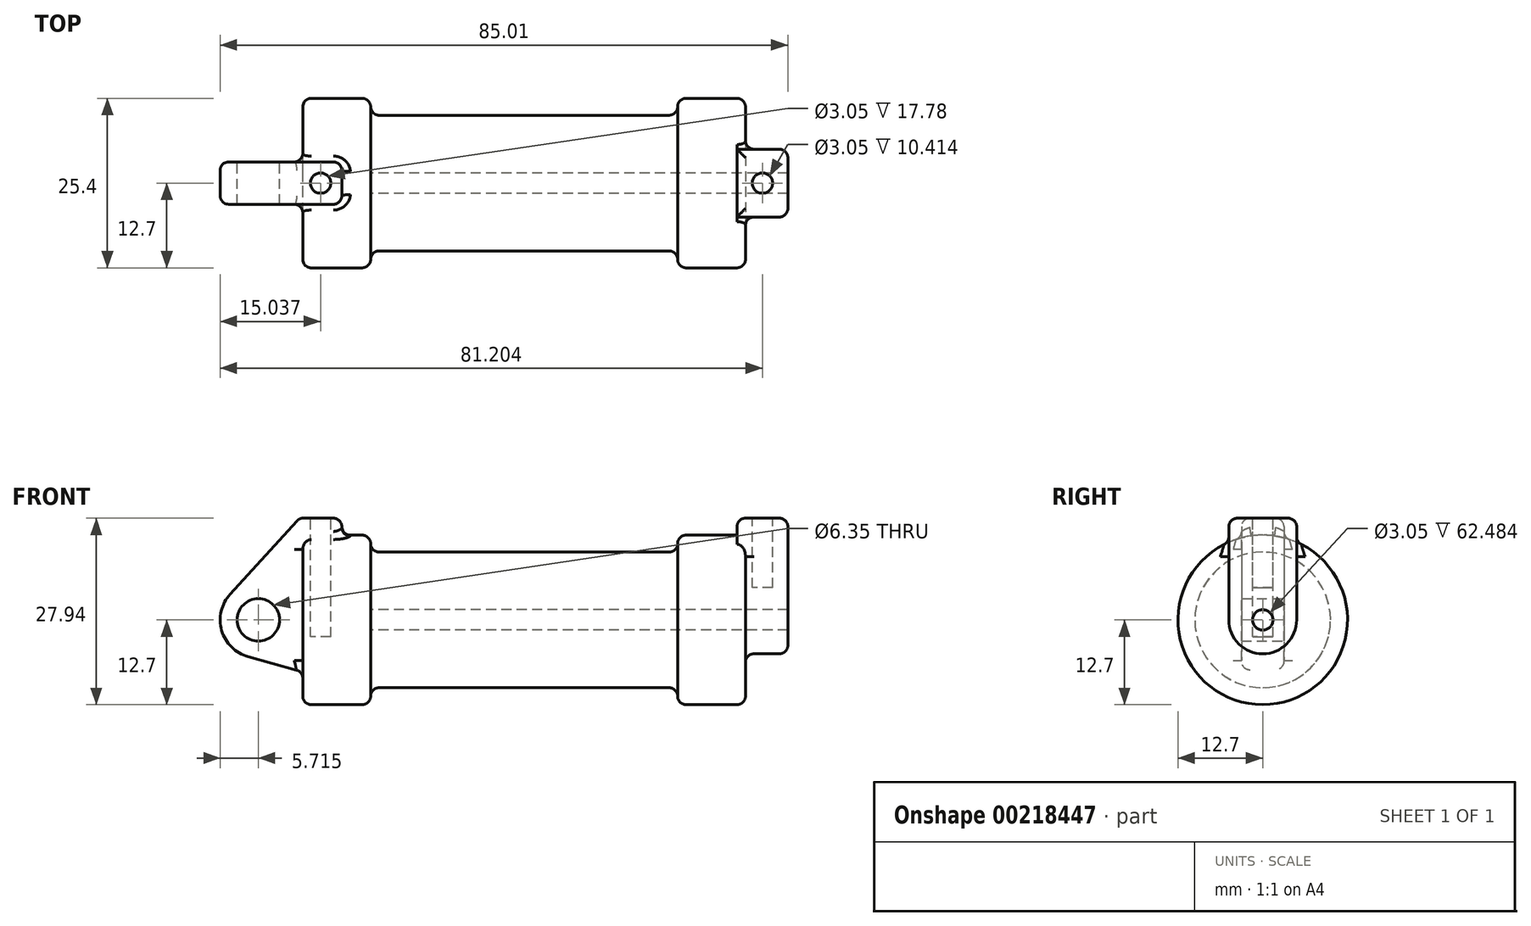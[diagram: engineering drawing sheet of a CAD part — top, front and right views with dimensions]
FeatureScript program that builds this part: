
annotation { "Feature Type Name" : "Feature", "Feature Type Description" : "" }
export const myFeature = defineFeature(function(context is Context, id is Id, definition is map)
    precondition{}
    {
        {
            var Q0;
            Q0=qCreatedBy(makeId("Front.planeOp"),FACE);
            var sketch = newSketch(context, id + "F0", { "sketchPlane" : qUnion([Q0])});
            skLineSegment(sketch, "E0", {"start": v(0, 0) * mm, "end": v(0, 12.7) * mm});
            skLineSegment(sketch, "E1", {"start": v(0, 12.7) * mm, "end": v(10.16, 12.7) * mm});
            skLineSegment(sketch, "E2", {"start": v(10.16, 12.7) * mm, "end": v(10.16, 10.16) * mm});
            skLineSegment(sketch, "E3", {"start": v(10.16, 10.16) * mm, "end": v(56.13, 10.16) * mm});
            skLineSegment(sketch, "E4", {"start": v(56.13, 10.16) * mm, "end": v(56.13, 12.7) * mm});
            skLineSegment(sketch, "E5", {"start": v(56.13, 12.7) * mm, "end": v(66.3, 12.7) * mm});
            skLineSegment(sketch, "E6", {"start": v(66.3, 12.7) * mm, "end": v(66.3, 0) * mm});
            skLineSegment(sketch, "E7", {"start": v(66.3, 0) * mm, "end": v(0, 0) * mm});
            skLineSegment(sketch, "E8", {"start": v(5.84, 15.24) * mm, "end": v(-0.5, 15.24) * mm});
            skLineSegment(sketch, "E9", {"start": v(-0.5, 15.24) * mm, "end": v(-10.88, 3.85) * mm});
            skLineSegment(sketch, "E10", {"start": v(0, 0) * mm, "end": v(-6.65, 0) * mm});
            skCircle(sketch, "E11", {"center": v(-6.65, 0) * mm, "radius": 5.72 * mm});
            skCircle(sketch, "E12", {"center": v(-6.65, 0) * mm, "radius": 3.18 * mm});
            skLineSegment(sketch, "E13", {"start": v(5.84, 15.24) * mm, "end": v(5.84, -9.4) * mm});
            skLineSegment(sketch, "E14", {"start": v(5.84, -9.4) * mm, "end": v(-8.18, -5.5) * mm});
            skSolve(sketch);
        }
        {
            var Q0;
            {var subQ0=sQuery(id+"F0.wireOp",EDGE,"E2");Q0=makeQuery(id+"F0.imprint","IMPRINT",FACE,{"disambiguationData":[TD([[makeQuery(id+"F0.imprint","IMPRINT",EDGE,{"derivedFrom":subQ0}),-1.0]])]});}
            var Q1;
            {var subQ0=sQuery(id+"F0.wireOp",EDGE,"E0");Q1=makeQuery(id+"F0.imprint","IMPRINT",FACE,{"disambiguationData":[TD([[makeQuery(id+"F0.imprint","IMPRINT",EDGE,{"derivedFrom":subQ0}),-1.0]])]});}
            var Q2;
            Q2=sQuery(id+"F0.wireOp",EDGE,"E7");
            revolve(context, id + "F1", {"entities" : qUnion([Q0, Q1]), "axis" : qUnion([Q2]), "revolveType" : RevolveType.FULL});
        }
        {
            var Q0;
            {var subQ3=sQuery(id+"F0.wireOp",EDGE,"E0");Q0=makeQuery(id+"F0.imprint","IMPRINT",FACE,{"disambiguationData":[TD([[makeQuery(id+"F0.imprint","IMPRINT",EDGE,{"derivedFrom":subQ3}),1.0]])]});}
            var Q1;
            {var subQ4=sQuery(id+"F0.wireOp",EDGE,"E12");Q1=makeQuery(id+"F0.imprint","IMPRINT",FACE,{"disambiguationData":[TD([[makeQuery(id+"F0.imprint","IMPRINT",EDGE,{"derivedFrom":subQ4}),-1.0]])]});}
            var Q2;
            {var subQ0=sQuery(id+"F0.wireOp",EDGE,"E14");Q2=makeQuery(id+"F0.imprint","IMPRINT",FACE,{"disambiguationData":[TD([[makeQuery(id+"F0.imprint","IMPRINT",EDGE,{"derivedFrom":subQ0}),-1.0]])]});}
            var Q3;
            {var subQ0=sQuery(id+"F0.wireOp",EDGE,"E0");Q3=makeQuery(id+"F0.imprint","IMPRINT",FACE,{"disambiguationData":[TD([[makeQuery(id+"F0.imprint","IMPRINT",EDGE,{"derivedFrom":subQ0}),-1.0]])]});}
            extrude(context, id + "F2", {"entities" : qUnion([Q0, Q1, Q2, Q3]), "operationType" : NewBodyOperationType.ADD, "endBound" : BoundingType.SYMMETRIC, "depth" : 6.35 * mm});
        }
        {
            var Q0;
            Q0=makeQuery(id+"F1.opRevolve","SWEPT_FACE",FACE,{"disambiguationData":[OSD([sQuery(id+"F0.wireOp",EDGE,"E6")])]});
            var sketch = newSketch(context, id + "F3", { "sketchPlane" : qUnion([Q0])});
            skCircle(sketch, "E15", {"center": v(0, 0) * mm, "radius": 1.52 * mm});
            skCircle(sketch, "E16", {"center": v(0, 0) * mm, "radius": 5.08 * mm});
            skLineSegment(sketch, "E17", {"start": v(-5.08, 0) * mm, "end": v(-5.08, 15.24) * mm});
            skLineSegment(sketch, "E18", {"start": v(-5.08, 15.24) * mm, "end": v(5.08, 15.24) * mm});
            skLineSegment(sketch, "E19", {"start": v(5.08, 15.24) * mm, "end": v(5.08, 0) * mm});
            skSolve(sketch);
        }
        {
            var Q0;
            {var subQ0=sQuery(id+"F3.wireOp",EDGE,"E18");Q0=makeQuery(id+"F3.imprint","IMPRINT",FACE,{"disambiguationData":[TD([[makeQuery(id+"F3.imprint","IMPRINT",EDGE,{"derivedFrom":subQ0}),-1.0]])]});}
            extrude(context, id + "F4", {"entities" : qUnion([Q0]), "operationType" : NewBodyOperationType.ADD, "oppositeDirection" : true, "depth" : 1.27 * mm});
        }
        {
            var Q0;
            {var subQ0=sQuery(id+"F3.wireOp",EDGE,"E18");Q0=makeQuery(id+"F3.imprint","IMPRINT",FACE,{"disambiguationData":[TD([[makeQuery(id+"F3.imprint","IMPRINT",EDGE,{"derivedFrom":subQ0}),-1.0]])]});}
            var Q1;
            {var subQ0=sQuery(id+"F3.wireOp",EDGE,"E17");var subQ1=sQuery(id+"F3.wireOp",EDGE,"E16");var subQ2=makeQuery(id+"F3.imprint","INTERSECT",VERTEX,{"derivedFrom":[subQ1,subQ0]});Q1=makeQuery(id+"F3.imprint","IMPRINT",FACE,{"disambiguationData":[TD([[makeQuery(id+"F3.imprint","IMPRINT",EDGE,{"disambiguationData":[TD([[subQ2,1.0]])],"derivedFrom":subQ1}),-1.0]])]});}
            var Q2;
            Q2=makeQuery(id+"F3.imprint","IMPRINT",FACE,{"disambiguationData":[TD([[makeQuery(id+"F3.imprint","IMPRINT",EDGE,{"derivedFrom":sQuery(id+"F3.wireOp",EDGE,"E15")}),-1.0]])]});
            extrude(context, id + "F5", {"entities" : qUnion([Q0, Q1, Q2]), "operationType" : NewBodyOperationType.ADD, "depth" : 6.35 * mm});
        }
        {
            var Q0;
            Q0=makeQuery(id+"F3.imprint","IMPRINT",FACE,{"disambiguationData":[TD([[makeQuery(id+"F3.imprint","IMPRINT",EDGE,{"derivedFrom":sQuery(id+"F3.wireOp",EDGE,"E15")}),1.0]])]});
            var Q1;
            Q1=makeQuery(id+"F1.opRevolve","SWEPT_FACE",FACE,{"disambiguationData":[OSD([sQuery(id+"F0.wireOp",EDGE,"E2")])]});
            extrude(context, id + "F6", {"entities" : qUnion([Q0]), "operationType" : NewBodyOperationType.REMOVE, "endBound" : BoundingType.UP_TO_SURFACE, "oppositeDirection" : true, "endBoundEntityFace" : qUnion([Q1]), "depth" : 25.4 * mm});
        }
        {
            var Q0;
            Q0=makeQuery(id+"F2.opExtrude","SWEPT_FACE",FACE,{"disambiguationData":[OSD([sQuery(id+"F0.wireOp",EDGE,"E8")])]});
            var sketch = newSketch(context, id + "F7", { "sketchPlane" : qUnion([Q0])});
            skCircle(sketch, "E20", {"center": v(2.67, 0) * mm, "radius": 1.52 * mm});
            skPoint(sketch, "E20.centerSnap0", {"position": v(-0.5, 0) * mm});
            skPoint(sketch, "E20.centerSnap1", {"position": v(2.67, 3.18) * mm});
            skSolve(sketch);
        }
        {
            var Q0;
            Q0 = qSketchRegion(id + "F7", true);
            extrude(context, id + "F8", {"entities" : qUnion([Q0]), "operationType" : NewBodyOperationType.REMOVE, "oppositeDirection" : true, "depth" : 17.78 * mm});
        }
        {
            var Q0;
            {var subQ0=sQuery(id+"F3.wireOp",EDGE,"E18");Q0=makeQuery(id+"F5.boolean.opBoolean","MERGE",FACE,{"derivedFrom":[makeQuery(id+"F4.opExtrude","SWEPT_FACE",FACE,{"disambiguationData":[OSD([subQ0])]}),makeQuery(id+"F5.opExtrude","SWEPT_FACE",FACE,{"disambiguationData":[OSD([subQ0])]})]});}
            var sketch = newSketch(context, id + "F9", { "sketchPlane" : qUnion([Q0])});
            skCircle(sketch, "E21", {"center": v(68.83, 0) * mm, "radius": 1.52 * mm});
            skPoint(sketch, "E21.centerSnap0", {"position": v(65.02, 0) * mm});
            skPoint(sketch, "E21.centerSnap1", {"position": v(68.83, 5.08) * mm});
            skSolve(sketch);
        }
        {
            var Q0;
            Q0 = qSketchRegion(id + "F9", true);
            extrude(context, id + "F10", {"entities" : qUnion([Q0]), "operationType" : NewBodyOperationType.REMOVE, "oppositeDirection" : true, "depth" : 10.4 * mm});
        }
        {
            var Q0;
            Q0=makeQuery(id+"F1.opRevolve","SWEPT_EDGE",EDGE,{"disambiguationData":[OSD([sQuery(id+"F0.wireOp",EDGE,"E2"),sQuery(id+"F0.wireOp",EDGE,"E3")])]});
            var Q1;
            Q1=makeQuery(id+"F1.opRevolve","SWEPT_EDGE",EDGE,{"disambiguationData":[OSD([sQuery(id+"F0.wireOp",EDGE,"E1"),sQuery(id+"F0.wireOp",EDGE,"E2")])]});
            var Q2;
            Q2=makeQuery(id+"F1.opRevolve","SWEPT_EDGE",EDGE,{"disambiguationData":[OSD([sQuery(id+"F0.wireOp",EDGE,"E3"),sQuery(id+"F0.wireOp",EDGE,"E4")])]});
            var Q3;
            Q3=makeQuery(id+"F1.opRevolve","SWEPT_EDGE",EDGE,{"disambiguationData":[OSD([sQuery(id+"F0.wireOp",EDGE,"E4"),sQuery(id+"F0.wireOp",EDGE,"E5")])]});
            var Q4;
            Q4=makeQuery(id+"F1.opRevolve","SWEPT_EDGE",EDGE,{"disambiguationData":[OSD([sQuery(id+"F0.wireOp",EDGE,"E5"),sQuery(id+"F0.wireOp",EDGE,"E6")])]});
            var Q5;
            Q5=makeQuery(id+"F1.opRevolve","SWEPT_EDGE",EDGE,{"disambiguationData":[OSD([sQuery(id+"F0.wireOp",EDGE,"E0"),sQuery(id+"F0.wireOp",EDGE,"E1")])]});
            fillet(context, id + "F11", {"entities" : qUnion([Q0, Q1, Q2, Q3, Q4, Q5]), "radius" : 1.27 * mm, "tangentPropagation" : true, "allowEdgeOverflow" : false});
        }
        {
            var Q0;
            Q0=makeQuery(id+"F1.boolean.opBoolean","INTERSECT",EDGE,{"derivedFrom":[makeQuery(id+"F2.opExtrude","CAP_FACE",FACE,{"disambiguationData":[OSD([sQuery(id+"F0.wireOp",EDGE,"E8"),sQuery(id+"F0.wireOp",EDGE,"E9"),sQuery(id+"F0.wireOp",EDGE,"E11"),sQuery(id+"F0.wireOp",EDGE,"E12"),sQuery(id+"F0.wireOp",EDGE,"E13"),sQuery(id+"F0.wireOp",EDGE,"E14")])],"isStart":false}),makeQuery(id+"F1.opRevolve","SWEPT_FACE",FACE,{"disambiguationData":[OSD([sQuery(id+"F0.wireOp",EDGE,"E1")])]})]});
            var Q1;
            Q1=makeQuery(id+"F1.opRevolve","SWEPT_FACE",FACE,{"disambiguationData":[OSD([sQuery(id+"F0.wireOp",EDGE,"E0")])]});
            var Q2;
            Q2=makeQuery(id+"F2.opExtrude","CAP_EDGE",EDGE,{"disambiguationData":[OSD([sQuery(id+"F0.wireOp",EDGE,"E9")])],"isStart":true});
            var Q3;
            Q3=makeQuery(id+"F2.opExtrude","CAP_EDGE",EDGE,{"disambiguationData":[OSD([sQuery(id+"F0.wireOp",EDGE,"E9")])],"isStart":false});
            var Q4;
            Q4=makeQuery(id+"F5.opExtrude","CAP_EDGE",EDGE,{"disambiguationData":[OSD([sQuery(id+"F3.wireOp",EDGE,"E17")])],"isStart":true});
            var Q5;
            Q5=makeQuery(id+"F5.opExtrude","CAP_EDGE",EDGE,{"disambiguationData":[OSD([sQuery(id+"F3.wireOp",EDGE,"E17")])],"isStart":false});
            var Q6;
            {var subQ0=sQuery(id+"F3.wireOp",EDGE,"E18");var subQ1=sQuery(id+"F3.wireOp",EDGE,"E17");Q6=makeQuery(id+"F5.boolean.opBoolean","MERGE",EDGE,{"derivedFrom":[makeQuery(id+"F4.opExtrude","SWEPT_EDGE",EDGE,{"disambiguationData":[OSD([subQ1,subQ0])]}),makeQuery(id+"F5.opExtrude","SWEPT_EDGE",EDGE,{"disambiguationData":[OSD([subQ1,subQ0])]})]});}
            var Q7;
            {var subQ0=sQuery(id+"F3.wireOp",EDGE,"E19");var subQ1=sQuery(id+"F3.wireOp",EDGE,"E18");Q7=makeQuery(id+"F5.boolean.opBoolean","MERGE",EDGE,{"derivedFrom":[makeQuery(id+"F4.opExtrude","SWEPT_EDGE",EDGE,{"disambiguationData":[OSD([subQ1,subQ0])]}),makeQuery(id+"F5.opExtrude","SWEPT_EDGE",EDGE,{"disambiguationData":[OSD([subQ1,subQ0])]})]});}
            var Q8;
            Q8=makeQuery(id+"F4.opExtrude","CAP_EDGE",EDGE,{"disambiguationData":[OSD([sQuery(id+"F3.wireOp",EDGE,"E18")])],"isStart":false});
            var Q9;
            Q9=makeQuery(id+"F5.opExtrude","CAP_EDGE",EDGE,{"disambiguationData":[OSD([sQuery(id+"F3.wireOp",EDGE,"E18")])],"isStart":false});
            var Q10;
            Q10=makeQuery(id+"F2.opExtrude","CAP_EDGE",EDGE,{"disambiguationData":[OSD([sQuery(id+"F0.wireOp",EDGE,"E8")])],"isStart":false});
            var Q11;
            Q11=makeQuery(id+"F2.opExtrude","SWEPT_EDGE",EDGE,{"disambiguationData":[OSD([sQuery(id+"F0.wireOp",EDGE,"E8"),sQuery(id+"F0.wireOp",EDGE,"E9")])]});
            var Q12;
            Q12=makeQuery(id+"F2.opExtrude","CAP_EDGE",EDGE,{"disambiguationData":[OSD([sQuery(id+"F0.wireOp",EDGE,"E8")])],"isStart":true});
            var Q13;
            Q13=makeQuery(id+"F2.opExtrude","SWEPT_EDGE",EDGE,{"disambiguationData":[OSD([sQuery(id+"F0.wireOp",EDGE,"E8"),sQuery(id+"F0.wireOp",EDGE,"E13")])]});
            var Q14;
            Q14=makeQuery(id+"F2.opExtrude","SWEPT_FACE",FACE,{"disambiguationData":[OSD([sQuery(id+"F0.wireOp",EDGE,"E13")])]});
            var Q15;
            Q15=makeQuery(id+"F4.opExtrude","CAP_EDGE",EDGE,{"disambiguationData":[OSD([sQuery(id+"F0.wireOp",EDGE,"E5"),sQuery(id+"F0.wireOp",EDGE,"E6")])],"isStart":false});
            fillet(context, id + "F12", {"entities" : qUnion([Q0, Q1, Q2, Q3, Q4, Q5, Q6, Q7, Q8, Q9, Q10, Q11, Q12, Q13, Q14, Q15]), "radius" : 1.27 * mm, "tangentPropagation" : true, "allowEdgeOverflow" : false});
        }
    });
